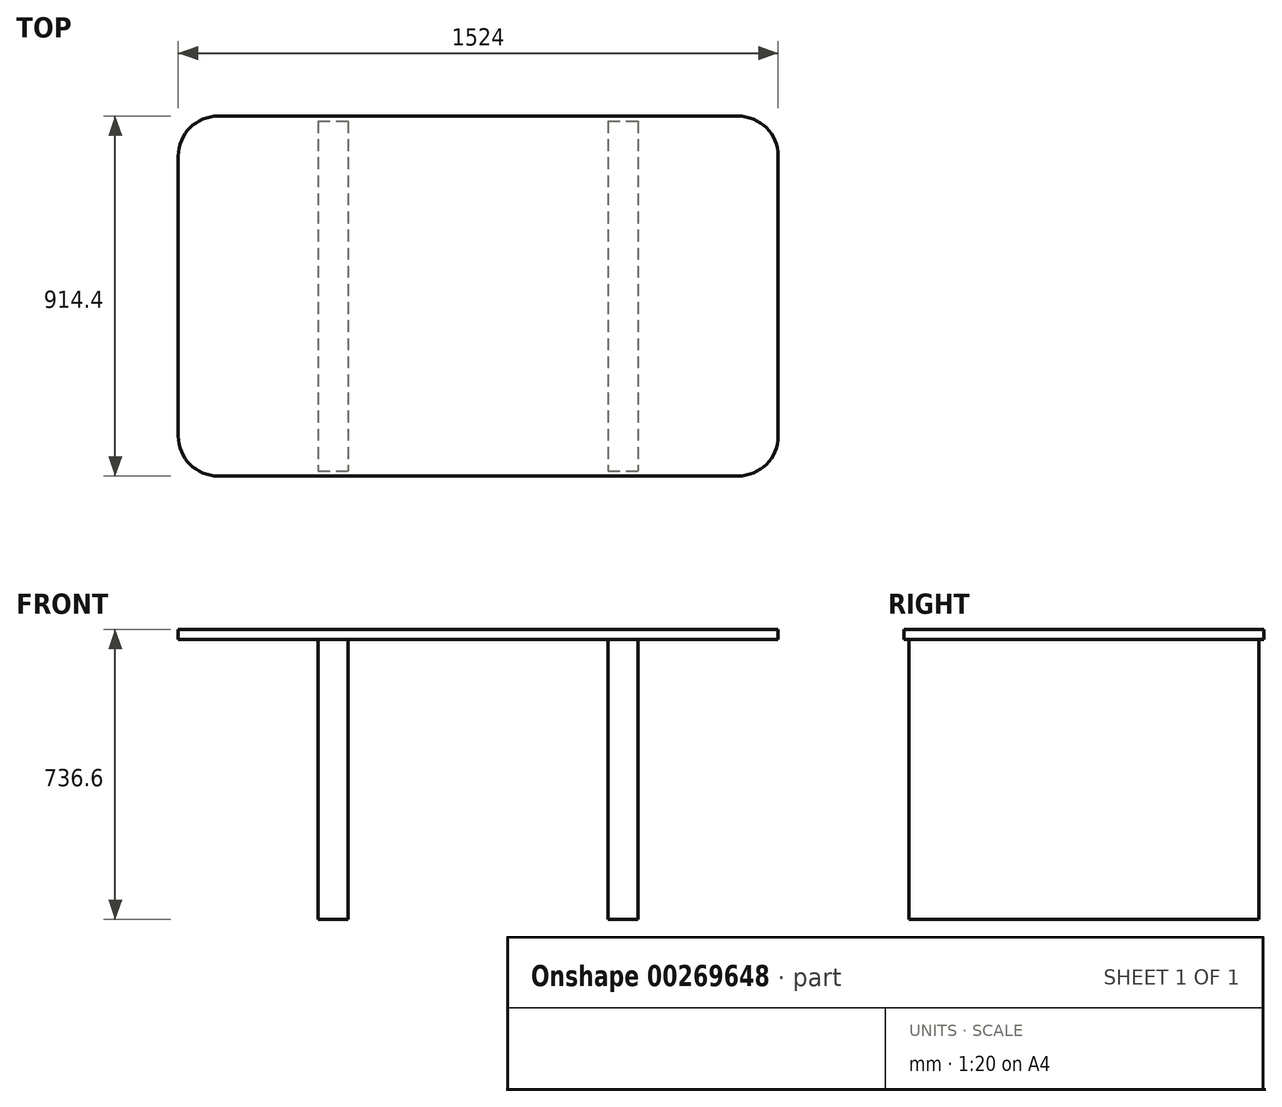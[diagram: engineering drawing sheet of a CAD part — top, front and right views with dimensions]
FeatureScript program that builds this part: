
annotation { "Feature Type Name" : "Feature", "Feature Type Description" : "" }
export const myFeature = defineFeature(function(context is Context, id is Id, definition is map)
    precondition{}
    {
        {
            var Q0;
            Q0=qCreatedBy(makeId("Top.planeOp"),FACE);
            var sketch = newSketch(context, id + "F0", { "sketchPlane" : qUnion([Q0])});
            skLineSegment(sketch, "E0.bottom", {"start": v(101.6, 0) * mm, "end": v(1422.4, 0) * mm});
            skLineSegment(sketch, "E0.top", {"start": v(101.6, 914.4) * mm, "end": v(1422.4, 914.4) * mm});
            skLineSegment(sketch, "E0.left", {"start": v(0, 101.6) * mm, "end": v(0, 812.8) * mm});
            skLineSegment(sketch, "E0.right", {"start": v(1524, 101.6) * mm, "end": v(1524, 812.8) * mm});
            skPoint(sketch, "E1.visualSharp", {"position": v(0, 914.4) * mm});
            skArc(sketch, "E1.filletArc", {"start": v(101.6, 914.4) * mm, "mid": v(29.76, 884.64) * mm, "end": v(0, 812.8) * mm});
            skPoint(sketch, "E2.visualSharp", {"position": v(0, 0) * mm});
            skArc(sketch, "E2.filletArc", {"start": v(0, 101.6) * mm, "mid": v(29.76, 29.76) * mm, "end": v(101.6, 0) * mm});
            skPoint(sketch, "E3.visualSharp", {"position": v(1524, 0) * mm});
            skArc(sketch, "E3.filletArc", {"start": v(1422.4, 0) * mm, "mid": v(1494.24, 29.76) * mm, "end": v(1524, 101.6) * mm});
            skPoint(sketch, "E4.visualSharp", {"position": v(1524, 914.4) * mm});
            skArc(sketch, "E4.filletArc", {"start": v(1524, 812.8) * mm, "mid": v(1494.24, 884.64) * mm, "end": v(1422.4, 914.4) * mm});
            skSolve(sketch);
        }
        {
            var Q0;
            Q0=qCreatedBy(makeId("Top.planeOp"),FACE);
            var sketch = newSketch(context, id + "F1", { "sketchPlane" : qUnion([Q0])});
            skLineSegment(sketch, "E5.bottom", {"start": v(355.6, 901.7) * mm, "end": v(431.8, 901.7) * mm});
            skLineSegment(sketch, "E5.top", {"start": v(355.6, 12.7) * mm, "end": v(431.8, 12.7) * mm});
            skLineSegment(sketch, "E5.left", {"start": v(355.6, 901.7) * mm, "end": v(355.6, 12.7) * mm});
            skLineSegment(sketch, "E5.right", {"start": v(431.8, 901.7) * mm, "end": v(431.8, 12.7) * mm});
            skLineSegment(sketch, "E6.bottom", {"start": v(1092.2, 901.7) * mm, "end": v(1168.4, 901.7) * mm});
            skLineSegment(sketch, "E6.top", {"start": v(1092.2, 12.7) * mm, "end": v(1168.4, 12.7) * mm});
            skLineSegment(sketch, "E6.left", {"start": v(1092.2, 901.7) * mm, "end": v(1092.2, 12.7) * mm});
            skLineSegment(sketch, "E6.right", {"start": v(1168.4, 901.7) * mm, "end": v(1168.4, 12.7) * mm});
            skSolve(sketch);
        }
        {
            var Q0;
            Q0=makeQuery(id+"F0.imprint","IMPRINT",FACE,{"disambiguationData":[TD([[makeQuery(id+"F0.imprint","IMPRINT",EDGE,{"derivedFrom":sQuery(id+"F0.wireOp",EDGE,"E0.bottom")}),1.0]])]});
            extrude(context, id + "F2", {"entities" : qUnion([Q0]), "depth" : 25.4 * mm});
        }
        {
            var Q0;
            Q0 = qSketchRegion(id + "F1", true);
            extrude(context, id + "F3", {"entities" : qUnion([Q0]), "operationType" : NewBodyOperationType.ADD, "oppositeDirection" : true, "depth" : 711.2 * mm});
        }
    });
